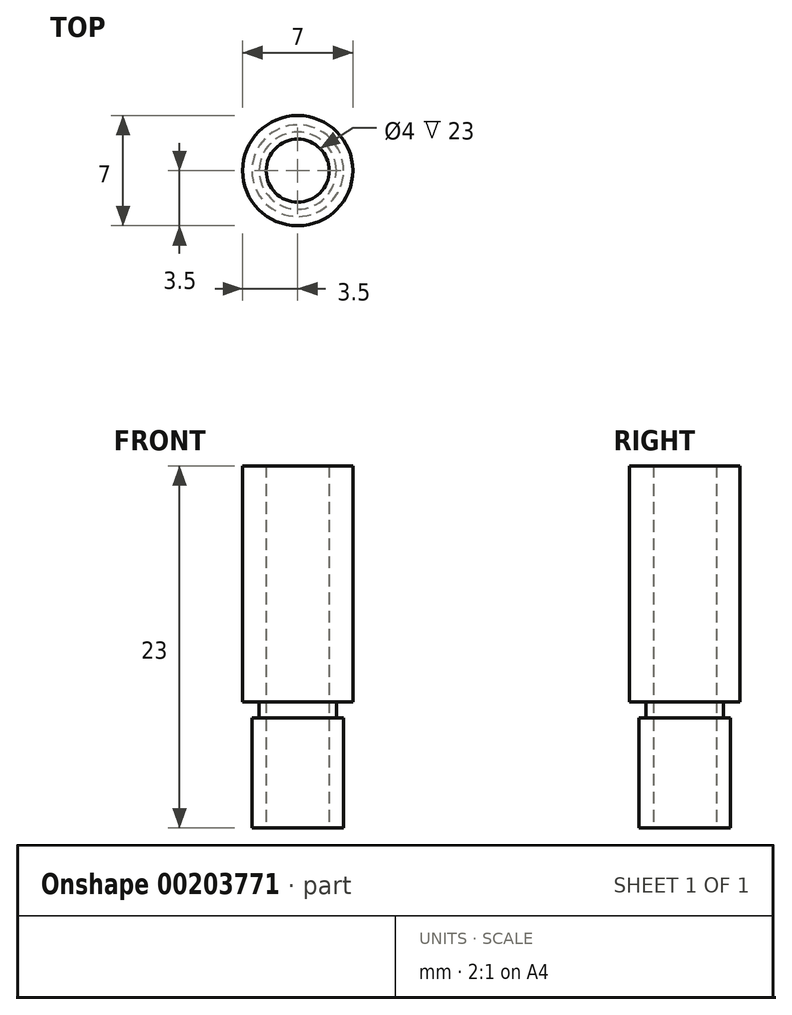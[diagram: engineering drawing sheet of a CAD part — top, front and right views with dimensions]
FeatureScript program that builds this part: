
annotation { "Feature Type Name" : "Feature", "Feature Type Description" : "" }
export const myFeature = defineFeature(function(context is Context, id is Id, definition is map)
    precondition{}
    {
        {
            var Q0;
            Q0=qCreatedBy(makeId("Top.planeOp"),FACE);
            var sketch = newSketch(context, id + "F0", { "sketchPlane" : qUnion([Q0])});
            skCircle(sketch, "E0", {"center": v(0, 0) * mm, "radius": 2 * mm});
            skCircle(sketch, "E1", {"center": v(0, 0) * mm, "radius": 3.5 * mm});
            skSolve(sketch);
        }
        {
            var Q0;
            Q0=makeQuery(id+"F0.imprint","IMPRINT",FACE,{"disambiguationData":[TD([[makeQuery(id+"F0.imprint","IMPRINT",EDGE,{"derivedFrom":sQuery(id+"F0.wireOp",EDGE,"E0")}),-1.0]])]});
            extrude(context, id + "F1", {"entities" : qUnion([Q0]), "depth" : 15 * mm});
        }
        {
            var Q0;
            Q0=qCreatedBy(makeId("Top.planeOp"),FACE);
            var sketch = newSketch(context, id + "F2", { "sketchPlane" : qUnion([Q0])});
            skCircle(sketch, "E2", {"center": v(0, 0) * mm, "radius": 2 * mm});
            skCircle(sketch, "E3", {"center": v(0, 0) * mm, "radius": 2.45 * mm});
            skSolve(sketch);
        }
        {
            var Q0;
            Q0=makeQuery(id+"F2.imprint","IMPRINT",FACE,{"disambiguationData":[TD([[makeQuery(id+"F2.imprint","IMPRINT",EDGE,{"derivedFrom":sQuery(id+"F2.wireOp",EDGE,"E2")}),-1.0]])]});
            extrude(context, id + "F3", {"entities" : qUnion([Q0]), "operationType" : NewBodyOperationType.ADD, "oppositeDirection" : true, "depth" : 1 * mm});
        }
        {
            var Q0;
            Q0=makeQuery(id+"F3.opExtrude","CAP_FACE",FACE,{"disambiguationData":[OSD([sQuery(id+"F2.wireOp",EDGE,"E2"),sQuery(id+"F2.wireOp",EDGE,"E3")])],"isStart":false});
            var sketch = newSketch(context, id + "F4", { "sketchPlane" : qUnion([Q0])});
            skCircle(sketch, "E4", {"center": v(0, 0) * mm, "radius": 2 * mm});
            skCircle(sketch, "E5", {"center": v(0, 0) * mm, "radius": 2.91 * mm});
            skSolve(sketch);
        }
        {
            var Q0;
            Q0 = qSketchRegion(id + "F4", true);
            extrude(context, id + "F5", {"entities" : qUnion([Q0]), "operationType" : NewBodyOperationType.ADD, "depth" : 7 * mm});
        }
    });
